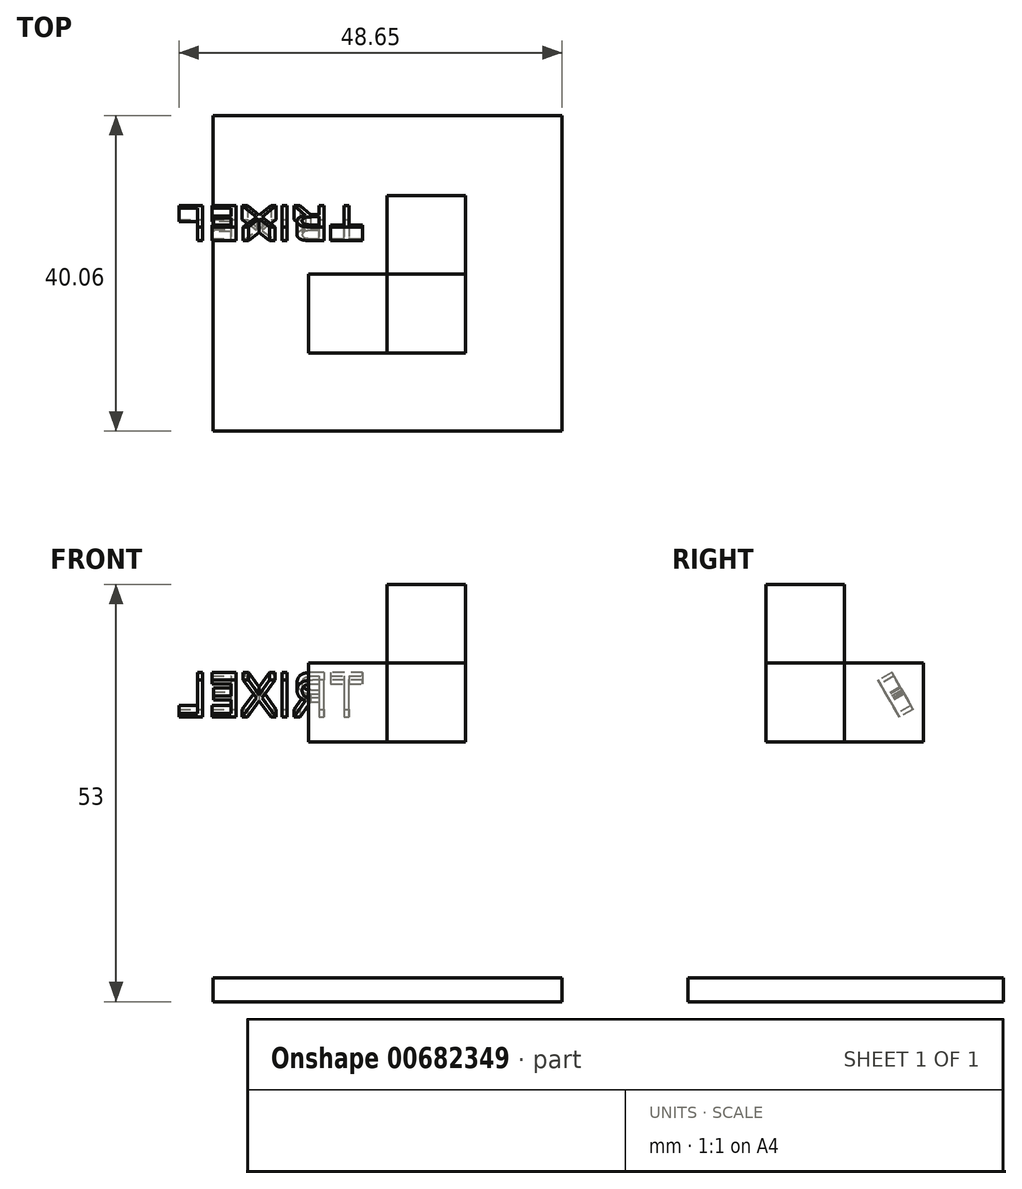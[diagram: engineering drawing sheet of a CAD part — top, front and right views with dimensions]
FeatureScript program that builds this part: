
annotation { "Feature Type Name" : "Feature", "Feature Type Description" : "" }
export const myFeature = defineFeature(function(context is Context, id is Id, definition is map)
    precondition{}
    {
        {
            var Q0;
            Q0=qCreatedBy(makeId("Front.planeOp"),FACE);
            var sketch = newSketch(context, id + "F0", { "sketchPlane" : qUnion([Q0])});
            skLineSegment(sketch, "E0.bottom", {"start": v(5, -5) * mm, "end": v(-5, -5) * mm});
            skLineSegment(sketch, "E0.top", {"start": v(5, 5) * mm, "end": v(-5, 5) * mm});
            skLineSegment(sketch, "E0.left", {"start": v(5, -5) * mm, "end": v(5, 5) * mm});
            skLineSegment(sketch, "E0.right", {"start": v(-5, -5) * mm, "end": v(-5, 5) * mm});
            skPoint(sketch, "E0.middle", {"position": v(0, 0) * mm});
            skSolve(sketch);
        }
        {
            var Q0;
            Q0=makeQuery(id+"F0.imprint","IMPRINT",FACE,{"disambiguationData":[TD([[makeQuery(id+"F0.imprint","IMPRINT",EDGE,{"derivedFrom":sQuery(id+"F0.wireOp",EDGE,"E0.bottom")}),-1.0]])]});
            extrude(context, id + "F1", {"entities" : qUnion([Q0]), "depth" : 10 * mm, "offsetDistance" : 25 * mm});
        }
        {
            var Q0;
            Q0=makeQuery(id+"F1.opExtrude","SWEPT_FACE",FACE,{"disambiguationData":[OSD([sQuery(id+"F0.wireOp",EDGE,"E0.right")])]});
            var sketch = newSketch(context, id + "F2", { "sketchPlane" : qUnion([Q0])});
            skLineSegment(sketch, "E1.bottom", {"start": v(10, 5) * mm, "end": v(20, 5) * mm});
            skLineSegment(sketch, "E1.top", {"start": v(10, 15) * mm, "end": v(20, 15) * mm});
            skLineSegment(sketch, "E1.left", {"start": v(10, 5) * mm, "end": v(10, 15) * mm});
            skLineSegment(sketch, "E1.right", {"start": v(20, 5) * mm, "end": v(20, 15) * mm});
            skSolve(sketch);
        }
        {
            var Q0;
            Q0=makeQuery(id+"F2.imprint","IMPRINT",FACE,{"disambiguationData":[TD([[makeQuery(id+"F2.imprint","IMPRINT",EDGE,{"derivedFrom":sQuery(id+"F2.wireOp",EDGE,"E1.bottom")}),1.0]])]});
            extrude(context, id + "F3", {"entities" : qUnion([Q0]), "oppositeDirection" : true, "depth" : 10 * mm, "offsetDistance" : 25 * mm});
        }
        {
            var Q0;
            Q0=makeQuery(id+"F3.opExtrude","CAP_FACE",FACE,{"disambiguationData":[OSD([sQuery(id+"F2.wireOp",EDGE,"E1.bottom"),sQuery(id+"F2.wireOp",EDGE,"E1.top"),sQuery(id+"F2.wireOp",EDGE,"E1.left"),sQuery(id+"F2.wireOp",EDGE,"E1.right")])],"isStart":true});
            var sketch = newSketch(context, id + "F4", { "sketchPlane" : qUnion([Q0])});
            skLineSegment(sketch, "E2.bottom", {"start": v(10, 5) * mm, "end": v(20, 5) * mm});
            skLineSegment(sketch, "E2.top", {"start": v(10, -5) * mm, "end": v(20, -5) * mm});
            skLineSegment(sketch, "E2.left", {"start": v(10, 5) * mm, "end": v(10, -5) * mm});
            skLineSegment(sketch, "E2.right", {"start": v(20, 5) * mm, "end": v(20, -5) * mm});
            skSolve(sketch);
        }
        {
            var Q0;
            Q0=makeQuery(id+"F4.imprint","IMPRINT",FACE,{"disambiguationData":[TD([[makeQuery(id+"F4.imprint","IMPRINT",EDGE,{"derivedFrom":sQuery(id+"F4.wireOp",EDGE,"E2.bottom")}),-1.0]])]});
            extrude(context, id + "F5", {"entities" : qUnion([Q0]), "depth" : 10 * mm, "offsetDistance" : 25 * mm});
        }
        {
            var Q0;
            Q0=makeQuery(id+"F5.opExtrude","SWEPT_FACE",FACE,{"disambiguationData":[OSD([sQuery(id+"F4.wireOp",EDGE,"E2.left")])]});
            cPlane(context, id + "F6", {"entities" : qUnion([Q0]), "cplaneType" : CPlaneType.OFFSET, "offset" : 5 * mm, "width" : 150 * mm, "height" : 150 * mm});
        }
        {
            var Q0;
            Q0=qCreatedBy(id+"F6.planeOp",FACE);
            var sketch = newSketch(context, id + "F7", { "sketchPlane" : qUnion([Q0])});
            skText(sketch, "E3", { "text": "TRIXEL\n", "fontName": "OpenSans-Regular.ttf"});
            const initialGuessF7  = {"E3": [0.00803, -0.00426, 1, 0, 0.00547]};
            skSetInitialGuess(sketch, initialGuessF7);
            skSolve(sketch);
        }
        {
            var Q0;
            Q0 = qSketchRegion(id + "F7", true);
            extrude(context, id + "F8", {"entities" : qUnion([Q0]), "depth" : 2 * mm, "offsetDistance" : 25 * mm});
        }
        {
            var Q0;
            Q0=makeQuery(id+"F8.opExtrude","SWEPT_BODY",BODY,{"disambiguationData":[OSD([sQuery(id+"F7.wireOp",EDGE,"E3.sketch_text.stroke-54"),sQuery(id+"F7.wireOp",EDGE,"E3.sketch_text.stroke-55"),sQuery(id+"F7.wireOp",EDGE,"E3.sketch_text.stroke-56"),sQuery(id+"F7.wireOp",EDGE,"E3.sketch_text.stroke-57"),sQuery(id+"F7.wireOp",EDGE,"E3.sketch_text.stroke-58"),sQuery(id+"F7.wireOp",EDGE,"E3.sketch_text.stroke-59")])]});
            var Q1;
            Q1=makeQuery(id+"F8.opExtrude","SWEPT_BODY",BODY,{"disambiguationData":[OSD([sQuery(id+"F7.wireOp",EDGE,"E3.sketch_text.stroke-42"),sQuery(id+"F7.wireOp",EDGE,"E3.sketch_text.stroke-43"),sQuery(id+"F7.wireOp",EDGE,"E3.sketch_text.stroke-44"),sQuery(id+"F7.wireOp",EDGE,"E3.sketch_text.stroke-45"),sQuery(id+"F7.wireOp",EDGE,"E3.sketch_text.stroke-46"),sQuery(id+"F7.wireOp",EDGE,"E3.sketch_text.stroke-47"),sQuery(id+"F7.wireOp",EDGE,"E3.sketch_text.stroke-48"),sQuery(id+"F7.wireOp",EDGE,"E3.sketch_text.stroke-49"),sQuery(id+"F7.wireOp",EDGE,"E3.sketch_text.stroke-50"),sQuery(id+"F7.wireOp",EDGE,"E3.sketch_text.stroke-51"),sQuery(id+"F7.wireOp",EDGE,"E3.sketch_text.stroke-52"),sQuery(id+"F7.wireOp",EDGE,"E3.sketch_text.stroke-53")])]});
            var Q2;
            Q2=makeQuery(id+"F8.opExtrude","SWEPT_BODY",BODY,{"disambiguationData":[OSD([sQuery(id+"F7.wireOp",EDGE,"E3.sketch_text.stroke-26"),sQuery(id+"F7.wireOp",EDGE,"E3.sketch_text.stroke-27"),sQuery(id+"F7.wireOp",EDGE,"E3.sketch_text.stroke-28"),sQuery(id+"F7.wireOp",EDGE,"E3.sketch_text.stroke-29")])]});
            var Q3;
            Q3=makeQuery(id+"F8.opExtrude","SWEPT_BODY",BODY,{"disambiguationData":[OSD([sQuery(id+"F7.wireOp",EDGE,"E3.sketch_text.stroke-8"),sQuery(id+"F7.wireOp",EDGE,"E3.sketch_text.stroke-9"),sQuery(id+"F7.wireOp",EDGE,"E3.sketch_text.stroke-10"),sQuery(id+"F7.wireOp",EDGE,"E3.sketch_text.stroke-11"),sQuery(id+"F7.wireOp",EDGE,"E3.sketch_text.stroke-12"),sQuery(id+"F7.wireOp",EDGE,"E3.sketch_text.stroke-13"),sQuery(id+"F7.wireOp",EDGE,"E3.sketch_text.stroke-14"),sQuery(id+"F7.wireOp",EDGE,"E3.sketch_text.stroke-15"),sQuery(id+"F7.wireOp",EDGE,"E3.sketch_text.stroke-16"),sQuery(id+"F7.wireOp",EDGE,"E3.sketch_text.stroke-17"),sQuery(id+"F7.wireOp",EDGE,"E3.sketch_text.stroke-18"),sQuery(id+"F7.wireOp",EDGE,"E3.sketch_text.stroke-19"),sQuery(id+"F7.wireOp",EDGE,"E3.sketch_text.stroke-20"),sQuery(id+"F7.wireOp",EDGE,"E3.sketch_text.stroke-21"),sQuery(id+"F7.wireOp",EDGE,"E3.sketch_text.stroke-22"),sQuery(id+"F7.wireOp",EDGE,"E3.sketch_text.stroke-23"),sQuery(id+"F7.wireOp",EDGE,"E3.sketch_text.stroke-24"),sQuery(id+"F7.wireOp",EDGE,"E3.sketch_text.stroke-25")])]});
            var Q4;
            Q4=makeQuery(id+"F8.opExtrude","SWEPT_BODY",BODY,{"disambiguationData":[OSD([sQuery(id+"F7.wireOp",EDGE,"E3.sketch_text.stroke-30"),sQuery(id+"F7.wireOp",EDGE,"E3.sketch_text.stroke-31"),sQuery(id+"F7.wireOp",EDGE,"E3.sketch_text.stroke-32"),sQuery(id+"F7.wireOp",EDGE,"E3.sketch_text.stroke-33"),sQuery(id+"F7.wireOp",EDGE,"E3.sketch_text.stroke-34"),sQuery(id+"F7.wireOp",EDGE,"E3.sketch_text.stroke-35"),sQuery(id+"F7.wireOp",EDGE,"E3.sketch_text.stroke-36"),sQuery(id+"F7.wireOp",EDGE,"E3.sketch_text.stroke-37"),sQuery(id+"F7.wireOp",EDGE,"E3.sketch_text.stroke-38"),sQuery(id+"F7.wireOp",EDGE,"E3.sketch_text.stroke-39"),sQuery(id+"F7.wireOp",EDGE,"E3.sketch_text.stroke-40"),sQuery(id+"F7.wireOp",EDGE,"E3.sketch_text.stroke-41")])]});
            var Q5;
            Q5=makeQuery(id+"F8.opExtrude","SWEPT_BODY",BODY,{"disambiguationData":[OSD([sQuery(id+"F7.wireOp",EDGE,"E3.sketch_text.stroke-0"),sQuery(id+"F7.wireOp",EDGE,"E3.sketch_text.stroke-1"),sQuery(id+"F7.wireOp",EDGE,"E3.sketch_text.stroke-2"),sQuery(id+"F7.wireOp",EDGE,"E3.sketch_text.stroke-3"),sQuery(id+"F7.wireOp",EDGE,"E3.sketch_text.stroke-4"),sQuery(id+"F7.wireOp",EDGE,"E3.sketch_text.stroke-5"),sQuery(id+"F7.wireOp",EDGE,"E3.sketch_text.stroke-6"),sQuery(id+"F7.wireOp",EDGE,"E3.sketch_text.stroke-7")])]});
            var Q6;
            Q6=makeQuery(id+"F5.opExtrude","SWEPT_EDGE",EDGE,{"disambiguationData":[OSD([sQuery(id+"F4.wireOp",EDGE,"E2.top"),sQuery(id+"F4.wireOp",EDGE,"E2.left")])]});
            transform(context, id + "F9", {"entities" : qUnion([Q0, Q1, Q2, Q3, Q4, Q5]), "transformType" : TransformType.ROTATION, "transformAxis" : qUnion([Q6]), "angle" : 30 * degree, "makeCopy" : false});
        }
        {
            var Q0;
            Q0=makeQuery(id+"F8.opExtrude","SWEPT_BODY",BODY,{"disambiguationData":[OSD([sQuery(id+"F7.wireOp",EDGE,"E3.sketch_text.stroke-0"),sQuery(id+"F7.wireOp",EDGE,"E3.sketch_text.stroke-1"),sQuery(id+"F7.wireOp",EDGE,"E3.sketch_text.stroke-2"),sQuery(id+"F7.wireOp",EDGE,"E3.sketch_text.stroke-3"),sQuery(id+"F7.wireOp",EDGE,"E3.sketch_text.stroke-4"),sQuery(id+"F7.wireOp",EDGE,"E3.sketch_text.stroke-5"),sQuery(id+"F7.wireOp",EDGE,"E3.sketch_text.stroke-6"),sQuery(id+"F7.wireOp",EDGE,"E3.sketch_text.stroke-7")])]});
            var Q1;
            Q1=makeQuery(id+"F8.opExtrude","SWEPT_BODY",BODY,{"disambiguationData":[OSD([sQuery(id+"F7.wireOp",EDGE,"E3.sketch_text.stroke-8"),sQuery(id+"F7.wireOp",EDGE,"E3.sketch_text.stroke-9"),sQuery(id+"F7.wireOp",EDGE,"E3.sketch_text.stroke-10"),sQuery(id+"F7.wireOp",EDGE,"E3.sketch_text.stroke-11"),sQuery(id+"F7.wireOp",EDGE,"E3.sketch_text.stroke-12"),sQuery(id+"F7.wireOp",EDGE,"E3.sketch_text.stroke-13"),sQuery(id+"F7.wireOp",EDGE,"E3.sketch_text.stroke-14"),sQuery(id+"F7.wireOp",EDGE,"E3.sketch_text.stroke-15"),sQuery(id+"F7.wireOp",EDGE,"E3.sketch_text.stroke-16"),sQuery(id+"F7.wireOp",EDGE,"E3.sketch_text.stroke-17"),sQuery(id+"F7.wireOp",EDGE,"E3.sketch_text.stroke-18"),sQuery(id+"F7.wireOp",EDGE,"E3.sketch_text.stroke-19"),sQuery(id+"F7.wireOp",EDGE,"E3.sketch_text.stroke-20"),sQuery(id+"F7.wireOp",EDGE,"E3.sketch_text.stroke-21"),sQuery(id+"F7.wireOp",EDGE,"E3.sketch_text.stroke-22"),sQuery(id+"F7.wireOp",EDGE,"E3.sketch_text.stroke-23"),sQuery(id+"F7.wireOp",EDGE,"E3.sketch_text.stroke-24"),sQuery(id+"F7.wireOp",EDGE,"E3.sketch_text.stroke-25")])]});
            var Q2;
            Q2=makeQuery(id+"F8.opExtrude","SWEPT_BODY",BODY,{"disambiguationData":[OSD([sQuery(id+"F7.wireOp",EDGE,"E3.sketch_text.stroke-26"),sQuery(id+"F7.wireOp",EDGE,"E3.sketch_text.stroke-27"),sQuery(id+"F7.wireOp",EDGE,"E3.sketch_text.stroke-28"),sQuery(id+"F7.wireOp",EDGE,"E3.sketch_text.stroke-29")])]});
            var Q3;
            Q3=makeQuery(id+"F8.opExtrude","SWEPT_BODY",BODY,{"disambiguationData":[OSD([sQuery(id+"F7.wireOp",EDGE,"E3.sketch_text.stroke-30"),sQuery(id+"F7.wireOp",EDGE,"E3.sketch_text.stroke-31"),sQuery(id+"F7.wireOp",EDGE,"E3.sketch_text.stroke-32"),sQuery(id+"F7.wireOp",EDGE,"E3.sketch_text.stroke-33"),sQuery(id+"F7.wireOp",EDGE,"E3.sketch_text.stroke-34"),sQuery(id+"F7.wireOp",EDGE,"E3.sketch_text.stroke-35"),sQuery(id+"F7.wireOp",EDGE,"E3.sketch_text.stroke-36"),sQuery(id+"F7.wireOp",EDGE,"E3.sketch_text.stroke-37"),sQuery(id+"F7.wireOp",EDGE,"E3.sketch_text.stroke-38"),sQuery(id+"F7.wireOp",EDGE,"E3.sketch_text.stroke-39"),sQuery(id+"F7.wireOp",EDGE,"E3.sketch_text.stroke-40"),sQuery(id+"F7.wireOp",EDGE,"E3.sketch_text.stroke-41")])]});
            var Q4;
            Q4=makeQuery(id+"F8.opExtrude","SWEPT_BODY",BODY,{"disambiguationData":[OSD([sQuery(id+"F7.wireOp",EDGE,"E3.sketch_text.stroke-42"),sQuery(id+"F7.wireOp",EDGE,"E3.sketch_text.stroke-43"),sQuery(id+"F7.wireOp",EDGE,"E3.sketch_text.stroke-44"),sQuery(id+"F7.wireOp",EDGE,"E3.sketch_text.stroke-45"),sQuery(id+"F7.wireOp",EDGE,"E3.sketch_text.stroke-46"),sQuery(id+"F7.wireOp",EDGE,"E3.sketch_text.stroke-47"),sQuery(id+"F7.wireOp",EDGE,"E3.sketch_text.stroke-48"),sQuery(id+"F7.wireOp",EDGE,"E3.sketch_text.stroke-49"),sQuery(id+"F7.wireOp",EDGE,"E3.sketch_text.stroke-50"),sQuery(id+"F7.wireOp",EDGE,"E3.sketch_text.stroke-51"),sQuery(id+"F7.wireOp",EDGE,"E3.sketch_text.stroke-52"),sQuery(id+"F7.wireOp",EDGE,"E3.sketch_text.stroke-53")])]});
            var Q5;
            Q5=makeQuery(id+"F8.opExtrude","SWEPT_BODY",BODY,{"disambiguationData":[OSD([sQuery(id+"F7.wireOp",EDGE,"E3.sketch_text.stroke-54"),sQuery(id+"F7.wireOp",EDGE,"E3.sketch_text.stroke-55"),sQuery(id+"F7.wireOp",EDGE,"E3.sketch_text.stroke-56"),sQuery(id+"F7.wireOp",EDGE,"E3.sketch_text.stroke-57"),sQuery(id+"F7.wireOp",EDGE,"E3.sketch_text.stroke-58"),sQuery(id+"F7.wireOp",EDGE,"E3.sketch_text.stroke-59")])]});
            transform(context, id + "F10", {"entities" : qUnion([Q0, Q1, Q2, Q3, Q4, Q5]), "transformType" : TransformType.TRANSLATION_3D, "dx" : 0 * mm, "dy" : 3 * mm, "dz" : 0 * mm, "makeCopy" : false});
        }
        {
            var Q0;
            Q0=makeQuery(id+"F1.opExtrude","SWEPT_FACE",FACE,{"disambiguationData":[OSD([sQuery(id+"F0.wireOp",EDGE,"E0.bottom")])]});
            cPlane(context, id + "F11", {"entities" : qUnion([Q0]), "cplaneType" : CPlaneType.OFFSET, "offset" : 30 * mm, "width" : 150 * mm, "height" : 150 * mm});
        }
        {
            var Q0;
            Q0=qCreatedBy(id+"F11.planeOp",FACE);
            var sketch = newSketch(context, id + "F12", { "sketchPlane" : qUnion([Q0])});
            skLineSegment(sketch, "E4.bottom", {"start": v(17.22, 29.9) * mm, "end": v(-27.1, 29.9) * mm});
            skLineSegment(sketch, "E4.top", {"start": v(17.22, -10.15) * mm, "end": v(-27.1, -10.15) * mm});
            skLineSegment(sketch, "E4.left", {"start": v(17.22, 29.9) * mm, "end": v(17.22, -10.15) * mm});
            skLineSegment(sketch, "E4.right", {"start": v(-27.1, 29.9) * mm, "end": v(-27.1, -10.15) * mm});
            skPoint(sketch, "E4.middle", {"position": v(-4.94, 9.88) * mm});
            skSolve(sketch);
        }
        {
            var Q0;
            Q0=makeQuery(id+"F12.imprint","IMPRINT",FACE,{"disambiguationData":[TD([[makeQuery(id+"F12.imprint","IMPRINT",EDGE,{"derivedFrom":sQuery(id+"F12.wireOp",EDGE,"E4.bottom")}),1.0]])]});
            extrude(context, id + "F13", {"entities" : qUnion([Q0]), "depth" : 3 * mm, "offsetDistance" : 25 * mm});
        }
    });
